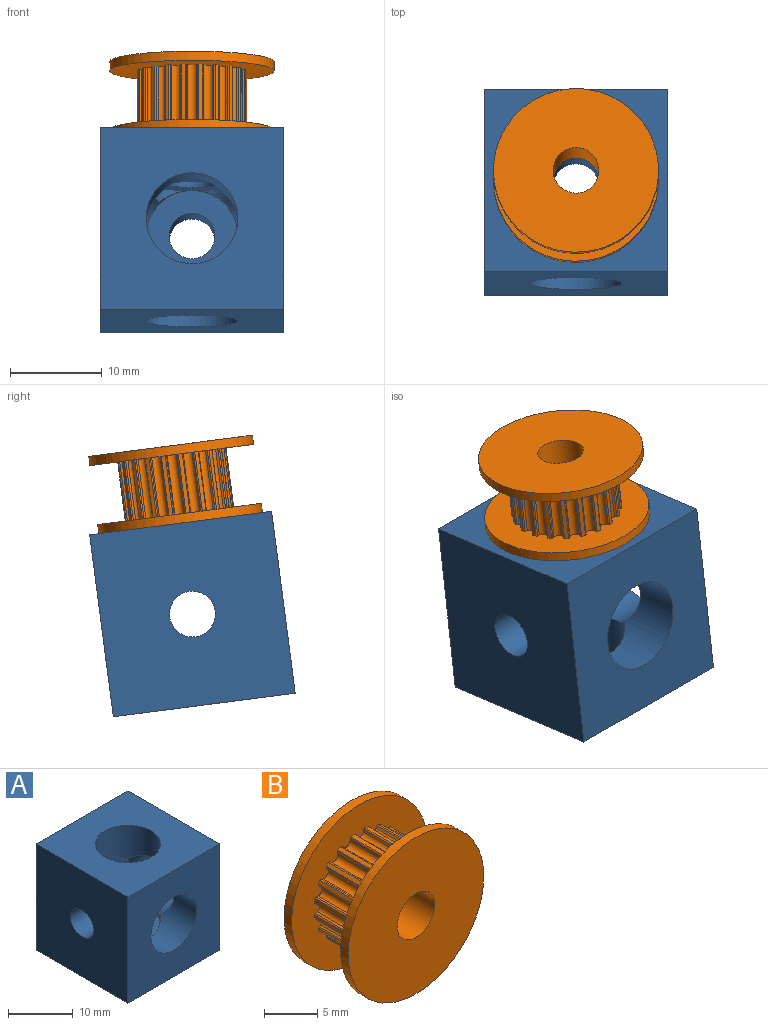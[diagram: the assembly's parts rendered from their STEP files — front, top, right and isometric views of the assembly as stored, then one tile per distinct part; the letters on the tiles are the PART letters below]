
ASSEMBLY  parts=2 mates=1
PART A: 27 faces, bbox 20x20x20 mm
  f0: cylinder r=5mm len=10mm, axis (0,-1,0), area 172.7mm2, adj f5,f7,f8,f13,f22,f24,f26
  f1: cylinder r=5mm len=5mm, axis (0,-1,0), area 3.9mm2, adj f9,f17,f21
  f2: cylinder r=5mm len=5mm, axis (0,-1,0), area 3.9mm2, adj f5,f17,f25
  f3: cylinder r=5mm len=5mm, axis (0,-1,0), area 3.9mm2, adj f5,f17,f26
  f4: cylinder r=5mm len=5mm, axis (0,-1,0), area 3.9mm2, adj f6,f17,f26
  f5: cylinder r=5mm len=10mm, axis (1,0,0), area 172.7mm2, adj f0,f2,f3,f10,f24,f25,f26
  f6: cylinder r=5mm len=5mm, axis (1,0,0), area 3.9mm2, adj f4,f18,f26
  f7: cylinder r=5mm len=5mm, axis (1,0,0), area 3.9mm2, adj f0,f18,f26
  f8: cylinder r=5mm len=5mm, axis (1,0,0), area 3.9mm2, adj f0,f18,f22
  f9: cylinder r=5mm len=5mm, axis (1,0,0), area 3.9mm2, adj f1,f18,f21
  f10: plane 20x20mm, normal (1,0,0), area 321.5mm2, adj f5,f11,f13,f14,f15
  f11: plane 20x20mm, normal (0,1,0), area 380.4mm2, adj f10,f12,f14,f15,f16
  f12: plane 20x20mm, normal (-1,0,0), area 380.4mm2, adj f11,f13,f14,f15,f19
  f13: plane 20x20mm, normal (0,-1,0), area 321.5mm2, adj f0,f10,f12,f14,f15
  f14: plane 20x20mm, normal (0,0,1), area 321.5mm2, adj f10,f11,f12,f13,f26
  f15: plane 20x20mm, normal (0,0,-1), area 380.4mm2, adj f10,f11,f12,f13,f20
  f16: cylinder r=2.5mm len=5mm, axis (0,-1,0), area 78.5mm2, adj f11,f17
  f17: plane 10x10mm, normal (0,-1,0), area 58.9mm2, adj f1,f2,f3,f4,f16
  f18: plane 10x10mm, normal (1,0,0), area 58.9mm2, adj f6,f7,f8,f9,f19
  f19: cylinder r=2.5mm len=5mm, axis (1,0,0), area 78.5mm2, adj f12,f18
  f20: cylinder r=2.5mm len=5mm, axis (0,0,1), area 78.5mm2, adj f15,f23
  f21: cylinder r=5mm len=5mm, axis (0,0,1), area 3.9mm2, adj f1,f9,f23
  f22: cylinder r=5mm len=5mm, axis (0,0,1), area 3.9mm2, adj f0,f8,f23
  f23: plane 10x10mm, normal (0,0,1), area 58.9mm2, adj f20,f21,f22,f24,f25
  f24: cylinder r=5mm len=5mm, axis (0,0,1), area 3.9mm2, adj f0,f5,f23
  f25: cylinder r=5mm len=5mm, axis (0,0,1), area 3.9mm2, adj f2,f5,f23
  f26: cylinder r=5mm len=10mm, axis (0,0,1), area 172.7mm2, adj f0,f3,f4,f5,f6,f7,f14
PART B: 127 faces, bbox 18x8.5x18 mm
  f0: cylinder r=1mm len=6.5mm, axis (0,1,0), area 1.6mm2, adj f1,f119,f120,f123
  f1: cylinder r=0.15mm len=6.5mm, axis (0,1,0), area 1.2mm2, adj f0,f2,f120,f123
  f2: cylinder r=6mm len=6.5mm, axis (0,1,0), area 2.9mm2, adj f1,f3,f120,f123
  f3: cylinder r=0.15mm len=6.5mm, axis (0,1,0), area 1.2mm2, adj f2,f4,f120,f123
  f4: cylinder r=1mm len=6.5mm, axis (0,1,0), area 1.6mm2, adj f3,f5,f120,f123
  f5: cylinder r=0.56mm len=6.5mm, axis (0,1,0), area 8.5mm2, adj f4,f6,f120,f123
  f6: cylinder r=1mm len=6.5mm, axis (0,1,0), area 1.6mm2, adj f5,f7,f120,f123
  f7: cylinder r=0.15mm len=6.5mm, axis (0,1,0), area 1.2mm2, adj f6,f8,f120,f123
  f8: cylinder r=6mm len=6.5mm, axis (0,1,0), area 2.9mm2, adj f7,f9,f120,f123
  f9: cylinder r=0.15mm len=6.5mm, axis (0,1,0), area 1.2mm2, adj f8,f10,f120,f123
  f10: cylinder r=1mm len=6.5mm, axis (0,1,0), area 1.6mm2, adj f9,f11,f120,f123
  f11: cylinder r=0.56mm len=6.5mm, axis (0,1,0), area 8.5mm2, adj f10,f12,f120,f123
  f12: cylinder r=1mm len=6.5mm, axis (0,1,0), area 1.6mm2, adj f11,f13,f120,f123
  f13: cylinder r=0.15mm len=6.5mm, axis (0,1,0), area 1.2mm2, adj f12,f14,f120,f123
  f14: cylinder r=6mm len=6.5mm, axis (0,1,0), area 2.9mm2, adj f13,f15,f120,f123
  f15: cylinder r=0.15mm len=6.5mm, axis (0,1,0), area 1.2mm2, adj f14,f16,f120,f123
  f16: cylinder r=1mm len=6.5mm, axis (0,1,0), area 1.6mm2, adj f15,f17,f120,f123
  f17: cylinder r=0.56mm len=6.5mm, axis (0,1,0), area 8.5mm2, adj f16,f18,f120,f123
  f18: cylinder r=1mm len=6.5mm, axis (0,1,0), area 1.6mm2, adj f17,f19,f120,f123
  f19: cylinder r=0.15mm len=6.5mm, axis (0,1,0), area 1.2mm2, adj f18,f20,f120,f123
  f20: cylinder r=6mm len=6.5mm, axis (0,1,0), area 2.9mm2, adj f19,f21,f120,f123
  f21: cylinder r=0.15mm len=6.5mm, axis (0,1,0), area 1.2mm2, adj f20,f22,f120,f123
  f22: cylinder r=1mm len=6.5mm, axis (0,1,0), area 1.6mm2, adj f21,f23,f120,f123
  f23: cylinder r=0.56mm len=6.5mm, axis (0,1,0), area 8.5mm2, adj f22,f24,f120,f123
  f24: cylinder r=1mm len=6.5mm, axis (0,1,0), area 1.6mm2, adj f23,f25,f120,f123
  f25: cylinder r=0.15mm len=6.5mm, axis (0,1,0), area 1.2mm2, adj f24,f26,f120,f123
  f26: cylinder r=6mm len=6.5mm, axis (0,1,0), area 2.4mm2, adj f25,f27,f120,f123
  f27: cylinder r=0.15mm len=6.5mm, axis (0,1,0), area 1.7mm2, adj f26,f28,f120,f123
  f28: cylinder r=1mm len=6.5mm, axis (0,1,0), area 1.6mm2, adj f27,f29,f120,f123
  f29: cylinder r=0.56mm len=6.5mm, axis (0,1,0), area 8.5mm2, adj f28,f30,f120,f123
  f30: cylinder r=1mm len=6.5mm, axis (0,1,0), area 1.6mm2, adj f29,f31,f120,f123
  f31: cylinder r=0.15mm len=6.5mm, axis (0,1,0), area 1.2mm2, adj f30,f32,f120,f123
  f32: cylinder r=6mm len=6.5mm, axis (0,1,0), area 2.9mm2, adj f31,f33,f120,f123
  f33: cylinder r=0.15mm len=6.5mm, axis (0,1,0), area 1.2mm2, adj f32,f34,f120,f123
  f34: cylinder r=1mm len=6.5mm, axis (0,1,0), area 1.6mm2, adj f33,f35,f120,f123
  f35: cylinder r=0.56mm len=6.5mm, axis (0,1,0), area 8.5mm2, adj f34,f36,f120,f123
  f36: cylinder r=1mm len=6.5mm, axis (0,1,0), area 1.6mm2, adj f35,f37,f120,f123
  f37: cylinder r=0.15mm len=6.5mm, axis (0,1,0), area 1.2mm2, adj f36,f38,f120,f123
  f38: cylinder r=6mm len=6.5mm, axis (0,1,0), area 2.9mm2, adj f37,f39,f120,f123
  f39: cylinder r=0.15mm len=6.5mm, axis (0,1,0), area 1.2mm2, adj f38,f40,f120,f123
  f40: cylinder r=1mm len=6.5mm, axis (0,1,0), area 1.6mm2, adj f39,f41,f120,f123
  f41: cylinder r=0.56mm len=6.5mm, axis (0,1,0), area 8.5mm2, adj f40,f42,f120,f123
  f42: cylinder r=1mm len=6.5mm, axis (0,1,0), area 1.6mm2, adj f41,f43,f120,f123
  f43: cylinder r=0.15mm len=6.5mm, axis (0,1,0), area 1.2mm2, adj f42,f44,f120,f123
  f44: cylinder r=6mm len=6.5mm, axis (0,1,0), area 2.9mm2, adj f43,f45,f120,f123
  f45: cylinder r=0.15mm len=6.5mm, axis (0,1,0), area 1.2mm2, adj f44,f46,f120,f123
  f46: cylinder r=1mm len=6.5mm, axis (0,1,0), area 1.6mm2, adj f45,f47,f120,f123
  f47: cylinder r=0.56mm len=6.5mm, axis (0,1,0), area 8.5mm2, adj f46,f48,f120,f123
  f48: cylinder r=1mm len=6.5mm, axis (0,1,0), area 1.6mm2, adj f47,f49,f120,f123
  f49: cylinder r=0.15mm len=6.5mm, axis (0,1,0), area 1.2mm2, adj f48,f50,f120,f123
  f50: cylinder r=6mm len=6.5mm, axis (0,1,0), area 2.9mm2, adj f49,f51,f120,f123
  f51: cylinder r=0.15mm len=6.5mm, axis (0,1,0), area 1.2mm2, adj f50,f52,f120,f123
  f52: cylinder r=1mm len=6.5mm, axis (0,1,0), area 1.6mm2, adj f51,f53,f120,f123
  f53: cylinder r=0.56mm len=6.5mm, axis (0,1,0), area 8.5mm2, adj f52,f54,f120,f123
  f54: cylinder r=1mm len=6.5mm, axis (0,1,0), area 1.6mm2, adj f53,f55,f120,f123
  f55: cylinder r=0.15mm len=6.5mm, axis (0,1,0), area 1.2mm2, adj f54,f56,f120,f123
  f56: cylinder r=6mm len=6.5mm, axis (0,1,0), area 2.9mm2, adj f55,f57,f120,f123
  f57: cylinder r=0.15mm len=6.5mm, axis (0,1,0), area 1.2mm2, adj f56,f58,f120,f123
  f58: cylinder r=1mm len=6.5mm, axis (0,1,0), area 1.6mm2, adj f57,f59,f120,f123
  f59: cylinder r=0.56mm len=6.5mm, axis (0,1,0), area 8.5mm2, adj f58,f60,f120,f123
  f60: cylinder r=1mm len=6.5mm, axis (0,1,0), area 1.6mm2, adj f59,f61,f120,f123
  f61: cylinder r=0.15mm len=6.5mm, axis (0,1,0), area 1.2mm2, adj f60,f62,f120,f123
  f62: cylinder r=6mm len=6.5mm, axis (0,1,0), area 2.9mm2, adj f61,f63,f120,f123
  f63: cylinder r=0.15mm len=6.5mm, axis (0,1,0), area 1.2mm2, adj f62,f64,f120,f123
  f64: cylinder r=1mm len=6.5mm, axis (0,1,0), area 1.6mm2, adj f63,f65,f120,f123
  f65: cylinder r=0.56mm len=6.5mm, axis (0,1,0), area 8.5mm2, adj f64,f66,f120,f123
  f66: cylinder r=1mm len=6.5mm, axis (0,1,0), area 1.6mm2, adj f65,f67,f120,f123
  f67: cylinder r=0.15mm len=6.5mm, axis (0,1,0), area 1.2mm2, adj f66,f68,f120,f123
  f68: cylinder r=6mm len=6.5mm, axis (0,1,0), area 2.9mm2, adj f67,f69,f120,f123
  f69: cylinder r=0.15mm len=6.5mm, axis (0,1,0), area 1.2mm2, adj f68,f70,f120,f123
  f70: cylinder r=1mm len=6.5mm, axis (0,1,0), area 1.6mm2, adj f69,f71,f120,f123
  f71: cylinder r=0.56mm len=6.5mm, axis (0,1,0), area 8.5mm2, adj f70,f72,f120,f123
  f72: cylinder r=1mm len=6.5mm, axis (0,1,0), area 1.6mm2, adj f71,f73,f120,f123
  f73: cylinder r=0.15mm len=6.5mm, axis (0,1,0), area 1.2mm2, adj f72,f74,f120,f123
  f74: cylinder r=6mm len=6.5mm, axis (0,1,0), area 2.9mm2, adj f73,f75,f120,f123
  f75: cylinder r=0.15mm len=6.5mm, axis (0,1,0), area 1.2mm2, adj f74,f76,f120,f123
  f76: cylinder r=1mm len=6.5mm, axis (0,1,0), area 1.6mm2, adj f75,f77,f120,f123
  f77: cylinder r=0.56mm len=6.5mm, axis (0,1,0), area 8.5mm2, adj f76,f78,f120,f123
  f78: cylinder r=1mm len=6.5mm, axis (0,1,0), area 1.6mm2, adj f77,f79,f120,f123
  f79: cylinder r=0.15mm len=6.5mm, axis (0,1,0), area 1.2mm2, adj f78,f80,f120,f123
  f80: cylinder r=6mm len=6.5mm, axis (0,1,0), area 2.9mm2, adj f79,f81,f120,f123
  f81: cylinder r=0.15mm len=6.5mm, axis (0,1,0), area 1.2mm2, adj f80,f82,f120,f123
  f82: cylinder r=1mm len=6.5mm, axis (0,1,0), area 1.6mm2, adj f81,f83,f120,f123
  f83: cylinder r=0.56mm len=6.5mm, axis (0,1,0), area 8.5mm2, adj f82,f84,f120,f123
  f84: cylinder r=1mm len=6.5mm, axis (0,1,0), area 1.6mm2, adj f83,f85,f120,f123
  f85: cylinder r=0.15mm len=6.5mm, axis (0,1,0), area 1.2mm2, adj f84,f86,f120,f123
  f86: cylinder r=6mm len=6.5mm, axis (0,1,0), area 2.9mm2, adj f85,f87,f120,f123
  f87: cylinder r=0.15mm len=6.5mm, axis (0,1,0), area 1.2mm2, adj f86,f88,f120,f123
  f88: cylinder r=1mm len=6.5mm, axis (0,1,0), area 1.6mm2, adj f87,f89,f120,f123
  f89: cylinder r=0.56mm len=6.5mm, axis (0,1,0), area 8.5mm2, adj f88,f90,f120,f123
  f90: cylinder r=1mm len=6.5mm, axis (0,1,0), area 1.6mm2, adj f89,f91,f120,f123
  f91: cylinder r=0.15mm len=6.5mm, axis (0,1,0), area 1.2mm2, adj f90,f92,f120,f123
  f92: cylinder r=6mm len=6.5mm, axis (0,1,0), area 2.9mm2, adj f91,f93,f120,f123
  f93: cylinder r=0.15mm len=6.5mm, axis (0,1,0), area 1.2mm2, adj f92,f94,f120,f123
  f94: cylinder r=1mm len=6.5mm, axis (0,1,0), area 1.6mm2, adj f93,f95,f120,f123
  f95: cylinder r=0.56mm len=6.5mm, axis (0,1,0), area 8.5mm2, adj f94,f96,f120,f123
  f96: cylinder r=1mm len=6.5mm, axis (0,1,0), area 1.6mm2, adj f95,f97,f120,f123
  f97: cylinder r=0.15mm len=6.5mm, axis (0,1,0), area 1.2mm2, adj f96,f98,f120,f123
  f98: cylinder r=6mm len=6.5mm, axis (0,1,0), area 2.9mm2, adj f97,f99,f120,f123
  f99: cylinder r=0.15mm len=6.5mm, axis (0,1,0), area 1.2mm2, adj f98,f100,f120,f123
  f100: cylinder r=1mm len=6.5mm, axis (0,1,0), area 1.6mm2, adj f99,f101,f120,f123
  f101: cylinder r=0.56mm len=6.5mm, axis (0,1,0), area 8.5mm2, adj f100,f102,f120,f123
  f102: cylinder r=1mm len=6.5mm, axis (0,1,0), area 1.6mm2, adj f101,f103,f120,f123
  f103: cylinder r=0.15mm len=6.5mm, axis (0,1,0), area 1.2mm2, adj f102,f104,f120,f123
  f104: cylinder r=6mm len=6.5mm, axis (0,1,0), area 2.9mm2, adj f103,f105,f120,f123
  f105: cylinder r=0.15mm len=6.5mm, axis (0,1,0), area 1.2mm2, adj f104,f106,f120,f123
  f106: cylinder r=1mm len=6.5mm, axis (0,1,0), area 1.6mm2, adj f105,f107,f120,f123
  f107: cylinder r=0.56mm len=6.5mm, axis (0,1,0), area 8.5mm2, adj f106,f108,f120,f123
  f108: cylinder r=1mm len=6.5mm, axis (0,1,0), area 1.6mm2, adj f107,f109,f120,f123
  f109: cylinder r=0.15mm len=6.5mm, axis (0,1,0), area 1.2mm2, adj f108,f110,f120,f123
  f110: cylinder r=6mm len=6.5mm, axis (0,1,0), area 2.9mm2, adj f109,f111,f120,f123
  f111: cylinder r=0.15mm len=6.5mm, axis (0,1,0), area 1.2mm2, adj f110,f112,f120,f123
  f112: cylinder r=1mm len=6.5mm, axis (0,1,0), area 1.6mm2, adj f111,f113,f120,f123
  f113: cylinder r=0.56mm len=6.5mm, axis (0,1,0), area 8.5mm2, adj f112,f114,f120,f123
  f114: cylinder r=1mm len=6.5mm, axis (0,1,0), area 1.6mm2, adj f113,f115,f120,f123
  f115: cylinder r=0.15mm len=6.5mm, axis (0,1,0), area 1.2mm2, adj f114,f116,f120,f123
  f116: cylinder r=6mm len=6.5mm, axis (0,1,0), area 2.9mm2, adj f115,f117,f120,f123
  f117: cylinder r=0.15mm len=6.5mm, axis (0,1,0), area 1.2mm2, adj f116,f118,f120,f123
  f118: cylinder r=1mm len=6.5mm, axis (0,1,0), area 1.6mm2, adj f117,f119,f120,f123
  f119: cylinder r=0.56mm len=6.5mm, axis (0,1,0), area 8.5mm2, adj f0,f118,f120,f123
  f120: plane 18x18mm, normal (0,1,0), area 155.7mm2, adj f0,f1,f2,f3,f4,f5,f6,f7
  f121: cylinder r=9mm len=18mm, axis (0,1,0), area 56.5mm2, adj f120,f122
  f122: plane 18x18mm, normal (0,-1,0), area 234.8mm2, adj f121,f126
  f123: plane 18x18mm, normal (0,-1,0), area 155.7mm2, adj f0,f1,f2,f3,f4,f5,f6,f7
  f124: cylinder r=9mm len=18mm, axis (0,-1,0), area 56.5mm2, adj f123,f125
  f125: plane 18x18mm, normal (0,1,0), area 234.8mm2, adj f124,f126
  f126: cylinder r=2.5mm len=8.5mm, axis (0,-1,0), area 133.5mm2, adj f122,f125
PLACE A rot(axis=(0.71,-0.71,0.05),174.8deg) t=(-379.39,344.26,-5.26)mm
PLACE B rot(axis=(1,0,0),82.6deg) t=(-379.39,344.81,-1.05)mm
MATE fastened B.f2 <-> A.f20  axis (0,-0.13,-0.99) through (-379.39,344.26,-5.26)mm
